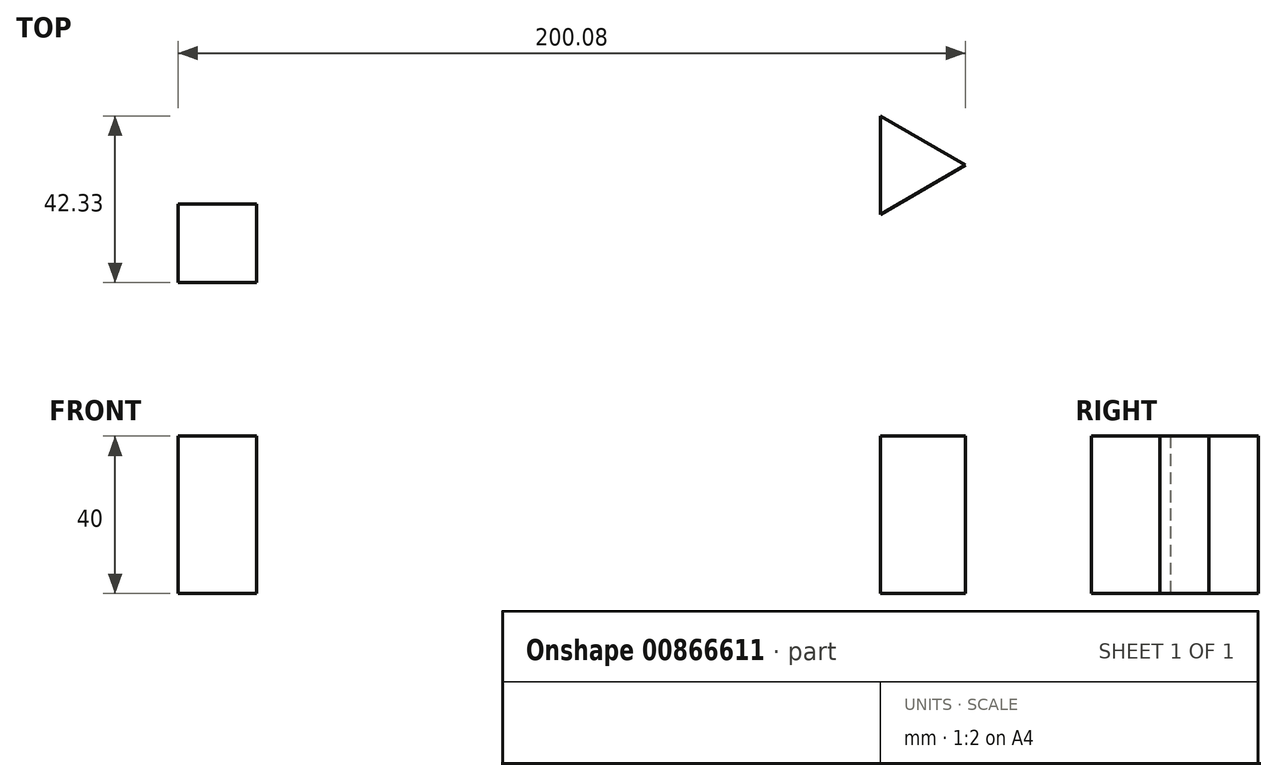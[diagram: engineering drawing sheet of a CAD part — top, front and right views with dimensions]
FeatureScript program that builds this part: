
annotation { "Feature Type Name" : "Feature", "Feature Type Description" : "" }
export const myFeature = defineFeature(function(context is Context, id is Id, definition is map)
    precondition{}
    {
        {
            var Q0;
            Q0=qCreatedBy(makeId("Top.planeOp"),FACE);
            var sketch = newSketch(context, id + "F0", { "sketchPlane" : qUnion([Q0])});
            skLineSegment(sketch, "E0.bottom", {"start": v(-157.98, 13.31) * mm, "end": v(-137.98, 13.31) * mm});
            skLineSegment(sketch, "E0.top", {"start": v(-157.98, -6.69) * mm, "end": v(-137.98, -6.69) * mm});
            skLineSegment(sketch, "E0.left", {"start": v(-157.98, 13.31) * mm, "end": v(-157.98, -6.69) * mm});
            skLineSegment(sketch, "E0.right", {"start": v(-137.98, 13.31) * mm, "end": v(-137.98, -6.69) * mm});
            skSolve(sketch);
        }
        {
            var Q0;
            Q0=makeQuery(id+"F0.imprint","IMPRINT",FACE,{"disambiguationData":[TD([[makeQuery(id+"F0.imprint","IMPRINT",EDGE,{"derivedFrom":sQuery(id+"F0.wireOp",EDGE,"E0.bottom")}),-1.0]])]});
            extrude(context, id + "F1", {"entities" : qUnion([Q0]), "depth" : 40 * mm, "offsetDistance" : 25 * mm});
        }
        {
            var Q0;
            Q0=qCreatedBy(makeId("Top.planeOp"),FACE);
            var sketch = newSketch(context, id + "F2", { "sketchPlane" : qUnion([Q0])});
            skCircle(sketch, "E1.cCircle", {"center": v(27.66, 23.14) * mm, "radius": 7.22 * mm, "construction": true});
            skLineSegment(sketch, "E1.0", {"start": v(42.1, 23.14) * mm, "end": v(20.45, 10.64) * mm});
            skLineSegment(sketch, "E1.1", {"start": v(20.45, 10.64) * mm, "end": v(20.45, 35.64) * mm});
            skLineSegment(sketch, "E1.2", {"start": v(20.45, 35.64) * mm, "end": v(42.1, 23.14) * mm});
            skPoint(sketch, "E1.0.midPoint", {"position": v(31.27, 16.9) * mm});
            skSolve(sketch);
        }
        {
            var Q0;
            Q0 = qSketchRegion(id + "F2", true);
            extrude(context, id + "F3", {"entities" : qUnion([Q0]), "depth" : 40 * mm, "offsetDistance" : 25 * mm});
        }
    });
